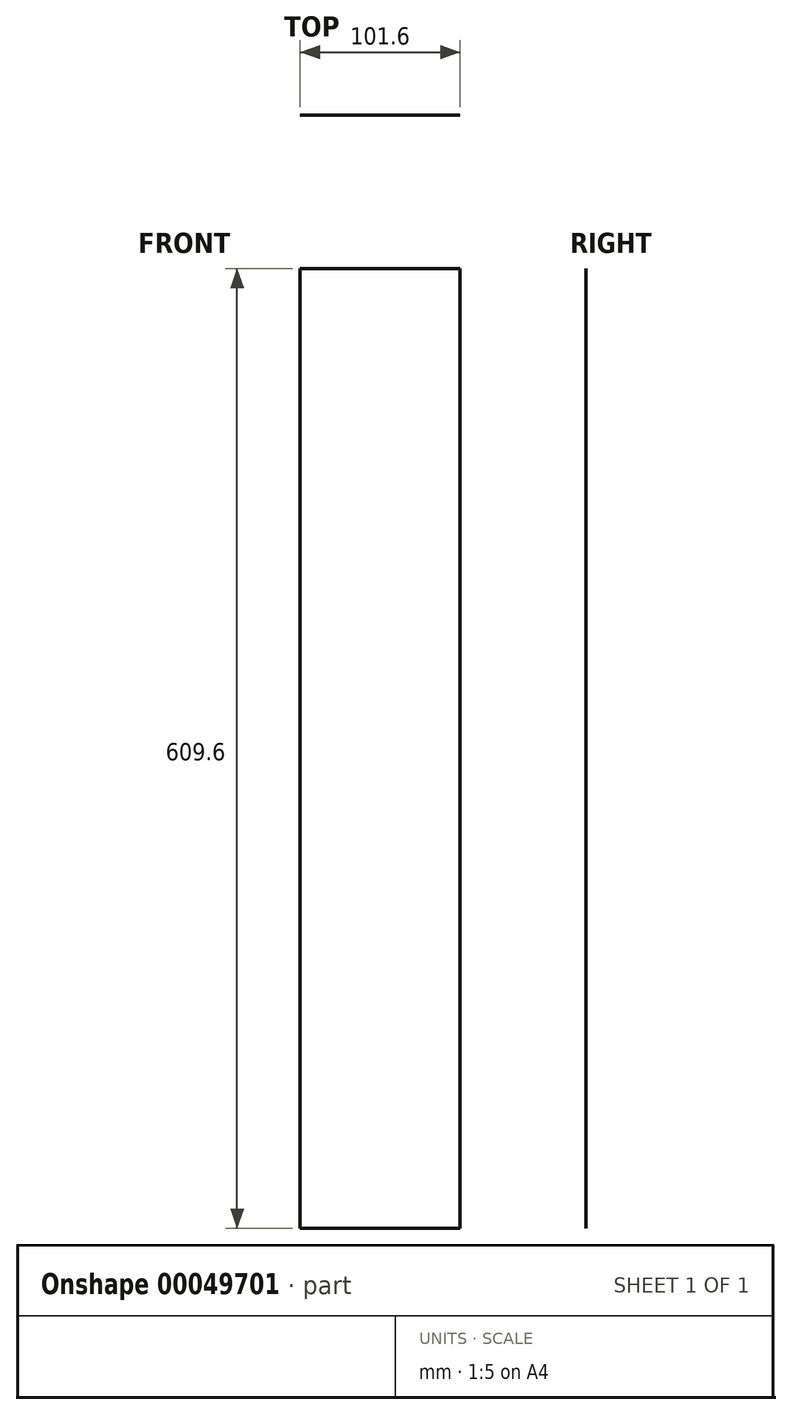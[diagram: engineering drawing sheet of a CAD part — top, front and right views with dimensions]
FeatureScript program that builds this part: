
annotation { "Feature Type Name" : "Feature", "Feature Type Description" : "" }
export const myFeature = defineFeature(function(context is Context, id is Id, definition is map)
    precondition{}
    {
        {
            var Q0;
            Q0=qCreatedBy(makeId("Top.planeOp"),FACE);
            cPlane(context, id + "F0", {"entities" : qUnion([Q0]), "cplaneType" : CPlaneType.OFFSET, "offset" : 76.2 * mm, "width" : 152.4 * mm, "height" : 152.4 * mm});
        }
        {
            var Q0;
            Q0=qCreatedBy(id+"F0.planeOp",FACE);
            var sketch = newSketch(context, id + "F1", { "sketchPlane" : qUnion([Q0])});
            skLineSegment(sketch, "E0.rect.bottom", {"start": v(50.8, 50.8) * mm, "end": v(-50.8, 50.8) * mm});
            skLineSegment(sketch, "E0.rect.top", {"start": v(50.8, -50.8) * mm, "end": v(-50.8, -50.8) * mm});
            skLineSegment(sketch, "E0.rect.left", {"start": v(50.8, 50.8) * mm, "end": v(50.8, -50.8) * mm});
            skLineSegment(sketch, "E0.rect.right", {"start": v(-50.8, 50.8) * mm, "end": v(-50.8, -50.8) * mm});
            skPoint(sketch, "E0.rect.middle", {"position": v(0, 0) * mm});
            skSolve(sketch);
        }
        {
            var Q0;
            Q0=sQuery(id+"F1.wireOp",EDGE,"E0.rect.top");
            extrude(context, id + "F2", {"bodyType" : ToolBodyType.SURFACE, "surfaceEntities" : qUnion([Q0]), "oppositeDirection" : true, "depth" : 609.6 * mm});
        }
    });
